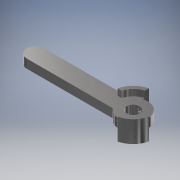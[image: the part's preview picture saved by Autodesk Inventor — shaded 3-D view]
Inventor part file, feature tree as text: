
AUTODESK INVENTOR PART (.ipt)
format: ipt  version: 2018 (Build 220112000, 112)  size: 176,128 bytes
history: native  units: mm (DEFAULTED — no unit token found)
features: extrude x3, sketch x2
ambient origin geometry x8: Origin, YZ Plane, XZ Plane, XY Plane, X Axis, Y Axis, Z Axis, Center Point
bodies: Solid1 (feature_tree)
feature tree (5):
  sketch  "Sketch1"  dims[d0=13.0mm d1=30.0mm]
  extrude  "Extrusion1"  Depth=30.0mm
  extrude  "Extrusion2"  Depth=42.0mm
  extrude  "Extrusion3"  Depth=4.5mm
  sketch  "Sketch2"  dims[d2=34.0mm d3=42.0mm d4=4.5mm d5=4.5mm d6=100.0mm d7=9.0mm d8=9.0mm d9=0.0mm d10=22.0mm d11=0.0mm d12=4.0mm d13=22.0mm d14=0.0mm]
